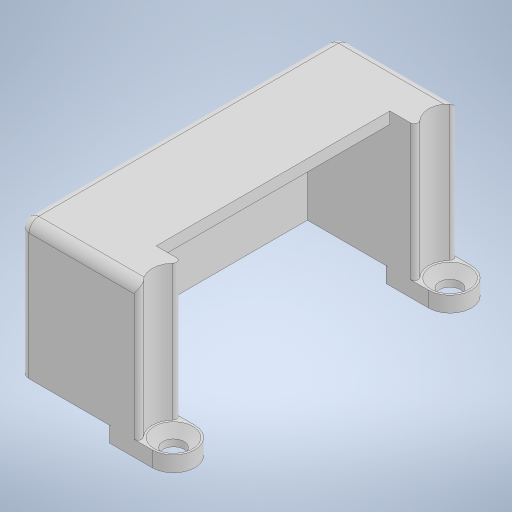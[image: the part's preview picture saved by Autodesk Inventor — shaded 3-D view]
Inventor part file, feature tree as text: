
AUTODESK INVENTOR PART (.ipt)
format: ipt  version: 2023 (Build 270158000, 158)  size: 274,944 bytes
history: native  units: mm
features: extrude x3, sketch x2, fillet x2, other x1, hole x1
ambient origin geometry x8: Origin, YZ Plane, XZ Plane, XY Plane, X Axis, Y Axis, Z Axis, Center Point
bodies: Body1 (feature_tree)
feature tree (9):
  other  "ソリッド1"
  sketch  "スケッチ1"
  extrude  "押し出し1"  Depth=28.5mm
  extrude  "押し出し2"  Depth=2.2mm
  extrude  "押し出し3"  Depth=4.4mm
  hole  "穴1"  [1 undecoded]
  fillet  "フィレット1"  Radius=1.2mm
  fillet  "フィレット2"  Radius=12.8mm
  sketch  "スケッチ2"
note: 1 required parameter value undecoded (feature->parameter linkage not recoverable at this tier; creation-order binding heuristic only, values carry confidence <= 0.55)
